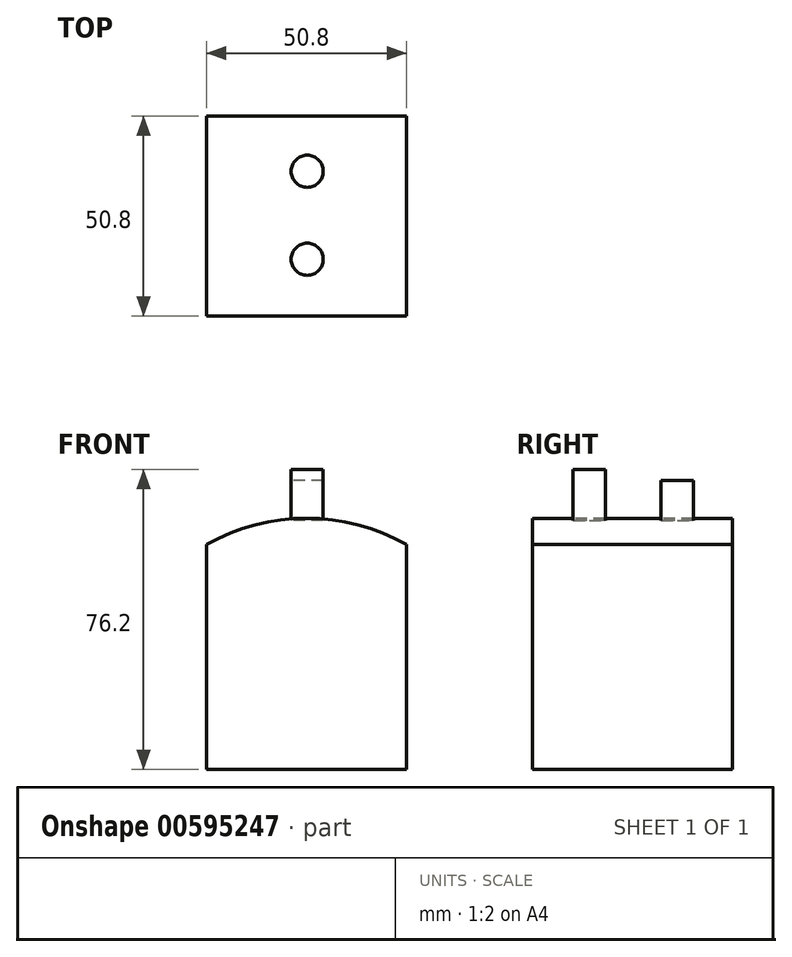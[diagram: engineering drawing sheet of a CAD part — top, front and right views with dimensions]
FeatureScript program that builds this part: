
annotation { "Feature Type Name" : "Feature", "Feature Type Description" : "" }
export const myFeature = defineFeature(function(context is Context, id is Id, definition is map)
    precondition{}
    {
        {
            var Q0;
            Q0=qCreatedBy(makeId("Top.planeOp"),FACE);
            var sketch = newSketch(context, id + "F0", { "sketchPlane" : qUnion([Q0])});
            skLineSegment(sketch, "E0.bottom", {"start": v(25.4, -25.4) * mm, "end": v(-25.4, -25.4) * mm});
            skLineSegment(sketch, "E0.top", {"start": v(25.4, 25.4) * mm, "end": v(-25.4, 25.4) * mm});
            skLineSegment(sketch, "E0.left", {"start": v(25.4, -25.4) * mm, "end": v(25.4, 25.4) * mm});
            skLineSegment(sketch, "E0.right", {"start": v(-25.4, -25.4) * mm, "end": v(-25.4, 25.4) * mm});
            skPoint(sketch, "E0.middle", {"position": v(0, 0) * mm});
            skSolve(sketch);
        }
        {
            var Q0;
            Q0=makeQuery(id+"F0.imprint","IMPRINT",FACE,{"disambiguationData":[TD([[makeQuery(id+"F0.imprint","IMPRINT",EDGE,{"derivedFrom":sQuery(id+"F0.wireOp",EDGE,"E0.bottom")}),-1.0]])]});
            extrude(context, id + "F1", {"entities" : qUnion([Q0]), "depth" : 57.15 * mm, "offsetDistance" : 25.4 * mm});
        }
        {
            var Q0;
            Q0=makeQuery(id+"F1.opExtrude","SWEPT_FACE",FACE,{"disambiguationData":[OSD([sQuery(id+"F0.wireOp",EDGE,"E0.bottom")])]});
            var sketch = newSketch(context, id + "F2", { "sketchPlane" : qUnion([Q0])});
            skArc(sketch, "E1", {"start": v(25.4, 57.15) * mm, "mid": v(0, 63.8) * mm, "end": v(-25.4, 57.15) * mm});
            skLineSegment(sketch, "E2", {"start": v(-25.4, 57.15) * mm, "end": v(25.4, 57.15) * mm});
            skSolve(sketch);
        }
        {
            var Q0;
            Q0=makeQuery(id+"F2.imprint","IMPRINT",FACE,{"disambiguationData":[TD([[makeQuery(id+"F2.imprint","IMPRINT",EDGE,{"derivedFrom":sQuery(id+"F2.wireOp",EDGE,"E1")}),1.0]])]});
            extrude(context, id + "F3", {"entities" : qUnion([Q0]), "operationType" : NewBodyOperationType.ADD, "oppositeDirection" : true, "depth" : 50.8 * mm, "offsetDistance" : 25.4 * mm});
        }
        {
            var Q0;
            Q0=qCreatedBy(makeId("Top.planeOp"),FACE);
            var sketch = newSketch(context, id + "F4", { "sketchPlane" : qUnion([Q0])});
            skCircle(sketch, "E3", {"center": v(-60.79, 88.08) * mm, "radius": 4.07 * mm});
            skSolve(sketch);
        }
        {
            var Q0;
            Q0 = qSketchRegion(id + "F4", true);
            extrude(context, id + "F5", {"entities" : qUnion([Q0]), "depth" : 10.16 * mm, "offsetDistance" : 25.4 * mm});
        }
        {
            var Q0;
            Q0=makeQuery(id+"F5.opExtrude","SWEPT_BODY",BODY,{"disambiguationData":[OSD([sQuery(id+"F4.wireOp",EDGE,"E3")])]});
            transform(context, id + "F6", {"entities" : qUnion([Q0]), "transformType" : TransformType.TRANSLATION_3D, "dx" : 60.96 * mm, "dy" : -74.93 * mm, "dz" : 63.25 * mm, "makeCopy" : false});
        }
        {
            var Q0;
            Q0=makeQuery(id+"F5.opExtrude","SWEPT_BODY",BODY,{"disambiguationData":[OSD([sQuery(id+"F4.wireOp",EDGE,"E3")])]});
            transform(context, id + "F7", {"entities" : qUnion([Q0]), "transformType" : TransformType.TRANSLATION_3D, "dx" : 0 * mm, "dy" : -24.13 * mm, "dz" : 0 * mm, "makeCopy" : true});
        }
        {
            var Q0;
            Q0=makeQuery(id+"F7.opPattern","COPY",FACE,{"derivedFrom":makeQuery(id+"F5.opExtrude","CAP_FACE",FACE,{"disambiguationData":[OSD([sQuery(id+"F4.wireOp",EDGE,"E3")])],"isStart":false}),"instanceName":"1"});
            extrude(context, id + "F8", {"entities" : qUnion([Q0]), "operationType" : NewBodyOperationType.ADD, "depth" : 2.8 * mm, "offsetDistance" : 25.4 * mm});
        }
        {
            var Q0;
            Q0=makeQuery(id+"F5.opExtrude","SWEPT_BODY",BODY,{"disambiguationData":[OSD([sQuery(id+"F4.wireOp",EDGE,"E3")])]});
            transform(context, id + "F9", {"entities" : qUnion([Q0]), "transformType" : TransformType.TRANSLATION_3D, "dx" : 0 * mm, "dy" : -1.78 * mm, "dz" : 0 * mm, "makeCopy" : false});
        }
    });
